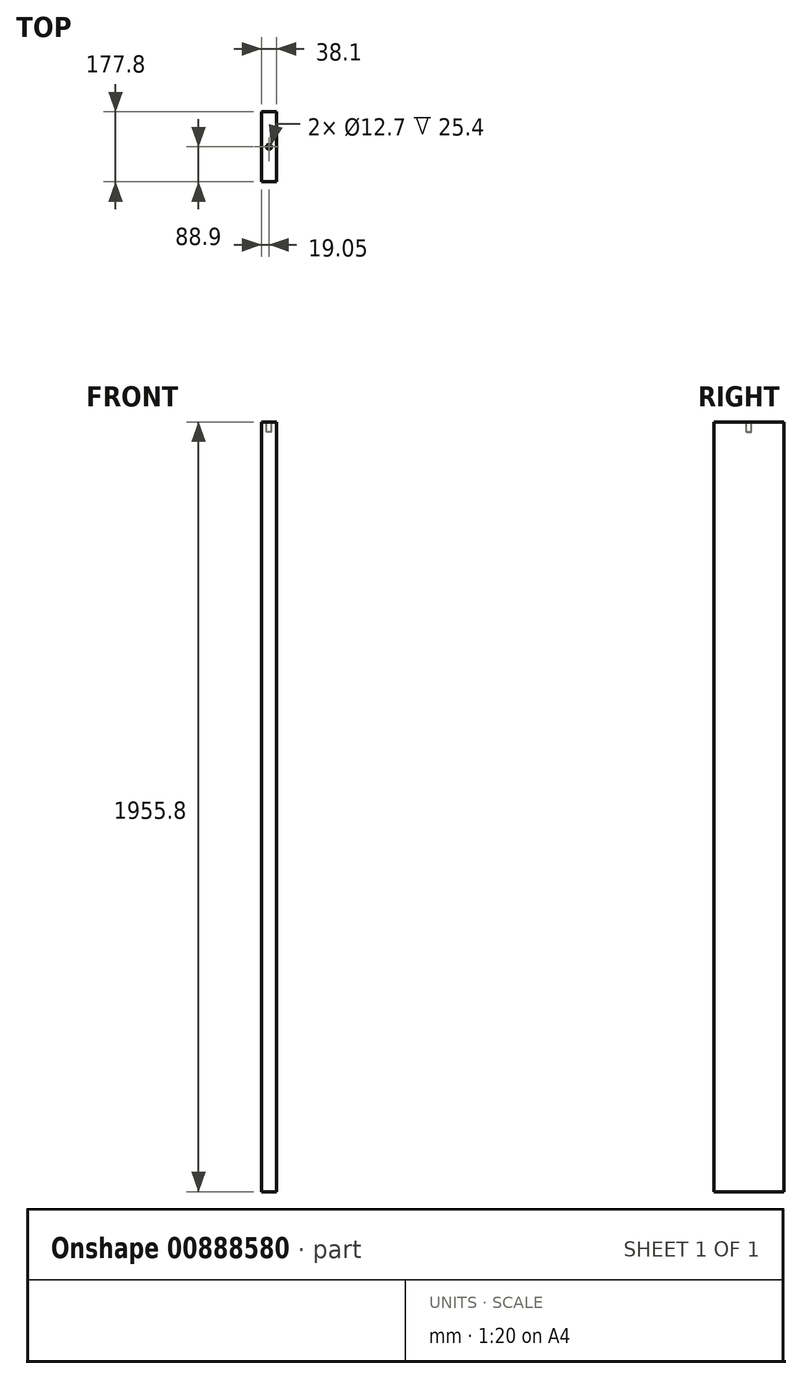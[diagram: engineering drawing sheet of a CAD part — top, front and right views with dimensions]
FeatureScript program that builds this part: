
annotation { "Feature Type Name" : "Feature", "Feature Type Description" : "" }
export const myFeature = defineFeature(function(context is Context, id is Id, definition is map)
    precondition{}
    {
        {
            var Q0;
            Q0=qCreatedBy(makeId("Top.planeOp"),FACE);
            var sketch = newSketch(context, id + "F0", { "sketchPlane" : qUnion([Q0])});
            skLineSegment(sketch, "E0.bottom", {"start": v(19.05, -88.9) * mm, "end": v(-19.05, -88.9) * mm});
            skLineSegment(sketch, "E0.top", {"start": v(19.05, 88.9) * mm, "end": v(-19.05, 88.9) * mm});
            skLineSegment(sketch, "E0.left", {"start": v(19.05, -88.9) * mm, "end": v(19.05, 88.9) * mm});
            skLineSegment(sketch, "E0.right", {"start": v(-19.05, -88.9) * mm, "end": v(-19.05, 88.9) * mm});
            skPoint(sketch, "E0.middle", {"position": v(0, 0) * mm});
            skSolve(sketch);
        }
        {
            var Q0;
            Q0=qCreatedBy(makeId("Top.planeOp"),FACE);
            var sketch = newSketch(context, id + "F1", { "sketchPlane" : qUnion([Q0])});
            skCircle(sketch, "E1", {"center": v(0, 0) * mm, "radius": 6.35 * mm});
            skSolve(sketch);
        }
        {
            var Q0;
            Q0=makeQuery(id+"F0.imprint","IMPRINT",FACE,{"disambiguationData":[TD([[makeQuery(id+"F0.imprint","IMPRINT",EDGE,{"derivedFrom":sQuery(id+"F0.wireOp",EDGE,"E0.bottom")}),-1.0]])]});
            extrude(context, id + "F2", {"entities" : qUnion([Q0]), "oppositeDirection" : true, "depth" : 1955.8 * mm, "offsetDistance" : 25.4 * mm});
        }
        {
            var Q0;
            Q0=makeQuery(id+"F1.imprint","IMPRINT",FACE,{"disambiguationData":[TD([[makeQuery(id+"F1.imprint","IMPRINT",EDGE,{"derivedFrom":sQuery(id+"F1.wireOp",EDGE,"E1")}),1.0]])]});
            extrude(context, id + "F3", {"entities" : qUnion([Q0]), "operationType" : NewBodyOperationType.REMOVE, "oppositeDirection" : true, "depth" : 25.4 * mm, "offsetDistance" : 25.4 * mm});
        }
    });
